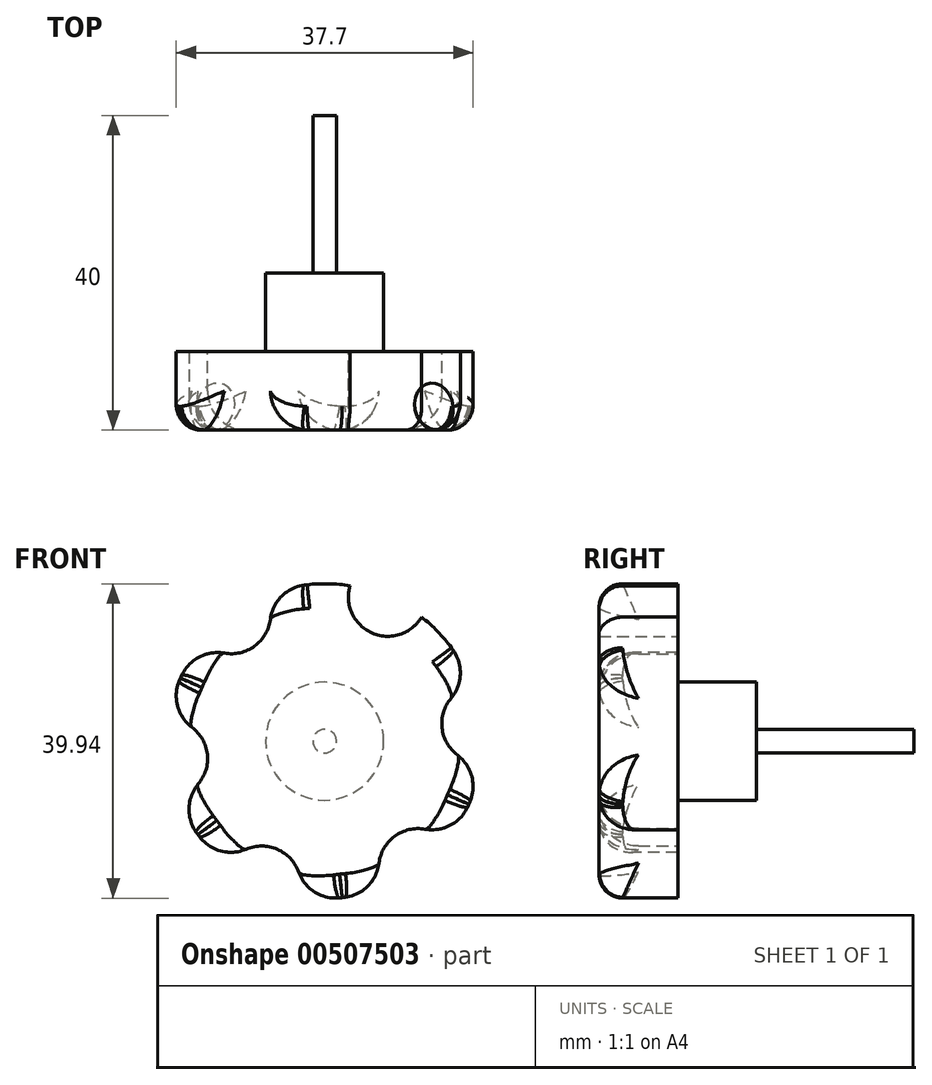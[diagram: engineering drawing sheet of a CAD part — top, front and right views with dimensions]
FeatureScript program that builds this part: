
annotation { "Feature Type Name" : "Feature", "Feature Type Description" : "" }
export const myFeature = defineFeature(function(context is Context, id is Id, definition is map)
    precondition{}
    {
        {
            var Q0;
            Q0=qCreatedBy(makeId("Front.planeOp"),FACE);
            var sketch = newSketch(context, id + "F0", { "sketchPlane" : qUnion([Q0])});
            skCircle(sketch, "E0", {"center": v(0, 0) * mm, "radius": 1.5 * mm});
            skSolve(sketch);
        }
        {
            var Q0;
            Q0 = qSketchRegion(id + "F0", true);
            extrude(context, id + "F1", {"entities" : qUnion([Q0]), "depth" : 20 * mm});
        }
        {
            var Q0;
            Q0=makeQuery(id+"F1.opExtrude","CAP_FACE",FACE,{"disambiguationData":[OSD([sQuery(id+"F0.wireOp",EDGE,"E0")])],"isStart":false});
            var sketch = newSketch(context, id + "F2", { "sketchPlane" : qUnion([Q0])});
            skCircle(sketch, "E1", {"center": v(0, 0) * mm, "radius": 7.5 * mm});
            skSolve(sketch);
        }
        {
            var Q0;
            Q0 = qSketchRegion(id + "F2", true);
            extrude(context, id + "F3", {"entities" : qUnion([Q0]), "operationType" : NewBodyOperationType.ADD, "depth" : 10 * mm});
        }
        {
            var Q0;
            Q0=makeQuery(id+"F3.opExtrude","CAP_FACE",FACE,{"disambiguationData":[OSD([sQuery(id+"F2.wireOp",EDGE,"E1")])],"isStart":false});
            var sketch = newSketch(context, id + "F4", { "sketchPlane" : qUnion([Q0])});
            skCircle(sketch, "E2", {"center": v(0, 0) * mm, "radius": 20 * mm});
            skSolve(sketch);
        }
        {
            var Q0;
            Q0 = qSketchRegion(id + "F4", true);
            extrude(context, id + "F5", {"entities" : qUnion([Q0]), "operationType" : NewBodyOperationType.ADD, "depth" : 10 * mm});
        }
        {
            var Q0;
            Q0=makeQuery(id+"F5.opExtrude","CAP_EDGE",EDGE,{"disambiguationData":[OSD([sQuery(id+"F4.wireOp",EDGE,"E2")])],"isStart":false});
            fillet(context, id + "F6", {"entities" : qUnion([Q0]), "radius" : 3 * mm, "tangentPropagation" : true, "allowEdgeOverflow" : false});
        }
        {
            var Q0;
            Q0=makeQuery(id+"F5.opExtrude","CAP_FACE",FACE,{"disambiguationData":[OSD([sQuery(id+"F4.wireOp",EDGE,"E2")])],"isStart":true});
            var sketch = newSketch(context, id + "F7", { "sketchPlane" : qUnion([Q0])});
            skPoint(sketch, "E3.0.midPoint", {"position": v(13.94, -10.27) * mm});
            skCircle(sketch, "E4", {"center": v(19.88, -2.22) * mm, "radius": 5 * mm});
            skCircle(sketch, "E5", {"center": v(8.01, -18.32) * mm, "radius": 5 * mm});
            skCircle(sketch, "E6", {"center": v(-11.86, -16.1) * mm, "radius": 5 * mm});
            skCircle(sketch, "E7", {"center": v(-19.88, 2.22) * mm, "radius": 5 * mm});
            skCircle(sketch, "E8", {"center": v(-8.01, 18.32) * mm, "radius": 5 * mm});
            skCircle(sketch, "E9", {"center": v(11.86, 16.1) * mm, "radius": 5 * mm});
            skSolve(sketch);
        }
        {
            var Q0;
            {var subQ0=sQuery(id+"F7.wireOp",EDGE,"E9");var subQ1=makeQuery(id+"F5.opExtrude","CAP_EDGE",EDGE,{"disambiguationData":[OSD([sQuery(id+"F4.wireOp",EDGE,"E2")])],"isStart":true});var subQ2=makeQuery(id+"F7.imprint","INTERSECT",VERTEX,{"disambiguationData":[OD(0.0)],"derivedFrom":[subQ1,subQ0]});Q0=makeQuery(id+"F7.imprint","IMPRINT",FACE,{"disambiguationData":[TD([[makeQuery(id+"F7.imprint","IMPRINT",EDGE,{"disambiguationData":[TD([[subQ2,1.0]])],"derivedFrom":subQ0}),1.0]])]});}
            var Q1;
            {var subQ0=sQuery(id+"F7.wireOp",EDGE,"E4");var subQ1=makeQuery(id+"F5.opExtrude","CAP_EDGE",EDGE,{"disambiguationData":[OSD([sQuery(id+"F4.wireOp",EDGE,"E2")])],"isStart":true});var subQ2=makeQuery(id+"F7.imprint","INTERSECT",VERTEX,{"disambiguationData":[OD(0.0)],"derivedFrom":[subQ1,subQ0]});Q1=makeQuery(id+"F7.imprint","IMPRINT",FACE,{"disambiguationData":[TD([[makeQuery(id+"F7.imprint","IMPRINT",EDGE,{"disambiguationData":[TD([[subQ2,1.0]])],"derivedFrom":subQ0}),1.0]])]});}
            var Q2;
            {var subQ0=sQuery(id+"F7.wireOp",EDGE,"E5");var subQ1=makeQuery(id+"F5.opExtrude","CAP_EDGE",EDGE,{"disambiguationData":[OSD([sQuery(id+"F4.wireOp",EDGE,"E2")])],"isStart":true});var subQ2=makeQuery(id+"F7.imprint","INTERSECT",VERTEX,{"disambiguationData":[OD(0.0)],"derivedFrom":[subQ1,subQ0]});Q2=makeQuery(id+"F7.imprint","IMPRINT",FACE,{"disambiguationData":[TD([[makeQuery(id+"F7.imprint","IMPRINT",EDGE,{"disambiguationData":[TD([[subQ2,-1.0]])],"derivedFrom":subQ0}),1.0]])]});}
            var Q3;
            {var subQ0=sQuery(id+"F7.wireOp",EDGE,"E6");var subQ1=makeQuery(id+"F5.opExtrude","CAP_EDGE",EDGE,{"disambiguationData":[OSD([sQuery(id+"F4.wireOp",EDGE,"E2")])],"isStart":true});var subQ2=makeQuery(id+"F7.imprint","INTERSECT",VERTEX,{"disambiguationData":[OD(0.0)],"derivedFrom":[subQ1,subQ0]});Q3=makeQuery(id+"F7.imprint","IMPRINT",FACE,{"disambiguationData":[TD([[makeQuery(id+"F7.imprint","IMPRINT",EDGE,{"disambiguationData":[TD([[subQ2,-1.0]])],"derivedFrom":subQ0}),1.0]])]});}
            var Q4;
            {var subQ0=sQuery(id+"F7.wireOp",EDGE,"E7");var subQ1=makeQuery(id+"F5.opExtrude","CAP_EDGE",EDGE,{"disambiguationData":[OSD([sQuery(id+"F4.wireOp",EDGE,"E2")])],"isStart":true});var subQ2=makeQuery(id+"F7.imprint","INTERSECT",VERTEX,{"disambiguationData":[OD(0.0)],"derivedFrom":[subQ1,subQ0]});Q4=makeQuery(id+"F7.imprint","IMPRINT",FACE,{"disambiguationData":[TD([[makeQuery(id+"F7.imprint","IMPRINT",EDGE,{"disambiguationData":[TD([[subQ2,-1.0]])],"derivedFrom":subQ0}),1.0]])]});}
            var Q5;
            {var subQ0=sQuery(id+"F7.wireOp",EDGE,"E8");var subQ1=makeQuery(id+"F5.opExtrude","CAP_EDGE",EDGE,{"disambiguationData":[OSD([sQuery(id+"F4.wireOp",EDGE,"E2")])],"isStart":true});var subQ2=makeQuery(id+"F7.imprint","INTERSECT",VERTEX,{"disambiguationData":[OD(0.0)],"derivedFrom":[subQ1,subQ0]});Q5=makeQuery(id+"F7.imprint","IMPRINT",FACE,{"disambiguationData":[TD([[makeQuery(id+"F7.imprint","IMPRINT",EDGE,{"disambiguationData":[TD([[subQ2,1.0]])],"derivedFrom":subQ0}),1.0]])]});}
            extrude(context, id + "F8", {"entities" : qUnion([Q0, Q1, Q2, Q3, Q4, Q5]), "operationType" : NewBodyOperationType.REMOVE, "oppositeDirection" : true, "depth" : 10 * mm});
        }
        {
            var Q0;
            {var subQ0=sQuery(id+"F7.wireOp",EDGE,"E5");var subQ1=sQuery(id+"F4.wireOp",EDGE,"E2");Q0=makeQuery(id+"F8.boolean.opBoolean","COPY",EDGE,{"derivedFrom":makeQuery(id+"F8.opExtrude","SWEPT_EDGE",EDGE,{"disambiguationData":[OSD([subQ1,subQ0]),TDD([makeQuery(id+"F7.imprint","INTERSECT",VERTEX,{"disambiguationData":[OD(0.0)],"derivedFrom":[makeQuery(id+"F5.opExtrude","CAP_EDGE",EDGE,{"disambiguationData":[OSD([subQ1])],"isStart":true}),subQ0]})])]})});}
            var Q1;
            {var subQ0=sQuery(id+"F7.wireOp",EDGE,"E4");var subQ1=sQuery(id+"F4.wireOp",EDGE,"E2");Q1=makeQuery(id+"F8.boolean.opBoolean","COPY",EDGE,{"derivedFrom":makeQuery(id+"F8.opExtrude","SWEPT_EDGE",EDGE,{"disambiguationData":[OSD([subQ1,subQ0]),TDD([makeQuery(id+"F7.imprint","INTERSECT",VERTEX,{"disambiguationData":[OD(0.0)],"derivedFrom":[makeQuery(id+"F5.opExtrude","CAP_EDGE",EDGE,{"disambiguationData":[OSD([subQ1])],"isStart":true}),subQ0]})])]})});}
            var Q2;
            {var subQ0=sQuery(id+"F7.wireOp",EDGE,"E9");var subQ1=sQuery(id+"F4.wireOp",EDGE,"E2");Q2=makeQuery(id+"F8.boolean.opBoolean","COPY",EDGE,{"derivedFrom":makeQuery(id+"F8.opExtrude","SWEPT_EDGE",EDGE,{"disambiguationData":[OSD([subQ1,subQ0]),TDD([makeQuery(id+"F7.imprint","INTERSECT",VERTEX,{"disambiguationData":[OD(0.0)],"derivedFrom":[makeQuery(id+"F5.opExtrude","CAP_EDGE",EDGE,{"disambiguationData":[OSD([subQ1])],"isStart":true}),subQ0]})])]})});}
            var Q3;
            {var subQ0=sQuery(id+"F7.wireOp",EDGE,"E8");var subQ1=sQuery(id+"F4.wireOp",EDGE,"E2");Q3=makeQuery(id+"F8.boolean.opBoolean","COPY",EDGE,{"derivedFrom":makeQuery(id+"F8.opExtrude","SWEPT_EDGE",EDGE,{"disambiguationData":[OSD([subQ1,subQ0]),TDD([makeQuery(id+"F7.imprint","INTERSECT",VERTEX,{"disambiguationData":[OD(0.0)],"derivedFrom":[makeQuery(id+"F5.opExtrude","CAP_EDGE",EDGE,{"disambiguationData":[OSD([subQ1])],"isStart":true}),subQ0]})])]})});}
            var Q4;
            {var subQ0=sQuery(id+"F7.wireOp",EDGE,"E7");var subQ1=sQuery(id+"F4.wireOp",EDGE,"E2");Q4=makeQuery(id+"F8.boolean.opBoolean","COPY",EDGE,{"derivedFrom":makeQuery(id+"F8.opExtrude","SWEPT_EDGE",EDGE,{"disambiguationData":[OSD([subQ1,subQ0]),TDD([makeQuery(id+"F7.imprint","INTERSECT",VERTEX,{"disambiguationData":[OD(1.0)],"derivedFrom":[makeQuery(id+"F5.opExtrude","CAP_EDGE",EDGE,{"disambiguationData":[OSD([subQ1])],"isStart":true}),subQ0]})])]})});}
            var Q5;
            {var subQ0=sQuery(id+"F7.wireOp",EDGE,"E6");var subQ1=sQuery(id+"F4.wireOp",EDGE,"E2");Q5=makeQuery(id+"F8.boolean.opBoolean","COPY",EDGE,{"derivedFrom":makeQuery(id+"F8.opExtrude","SWEPT_EDGE",EDGE,{"disambiguationData":[OSD([subQ1,subQ0]),TDD([makeQuery(id+"F7.imprint","INTERSECT",VERTEX,{"disambiguationData":[OD(1.0)],"derivedFrom":[makeQuery(id+"F5.opExtrude","CAP_EDGE",EDGE,{"disambiguationData":[OSD([subQ1])],"isStart":true}),subQ0]})])]})});}
            fillet(context, id + "F9", {"entities" : qUnion([Q0, Q1, Q2, Q3, Q4, Q5]), "radius" : 5 * mm, "tangentPropagation" : true, "allowEdgeOverflow" : false});
        }
    });
